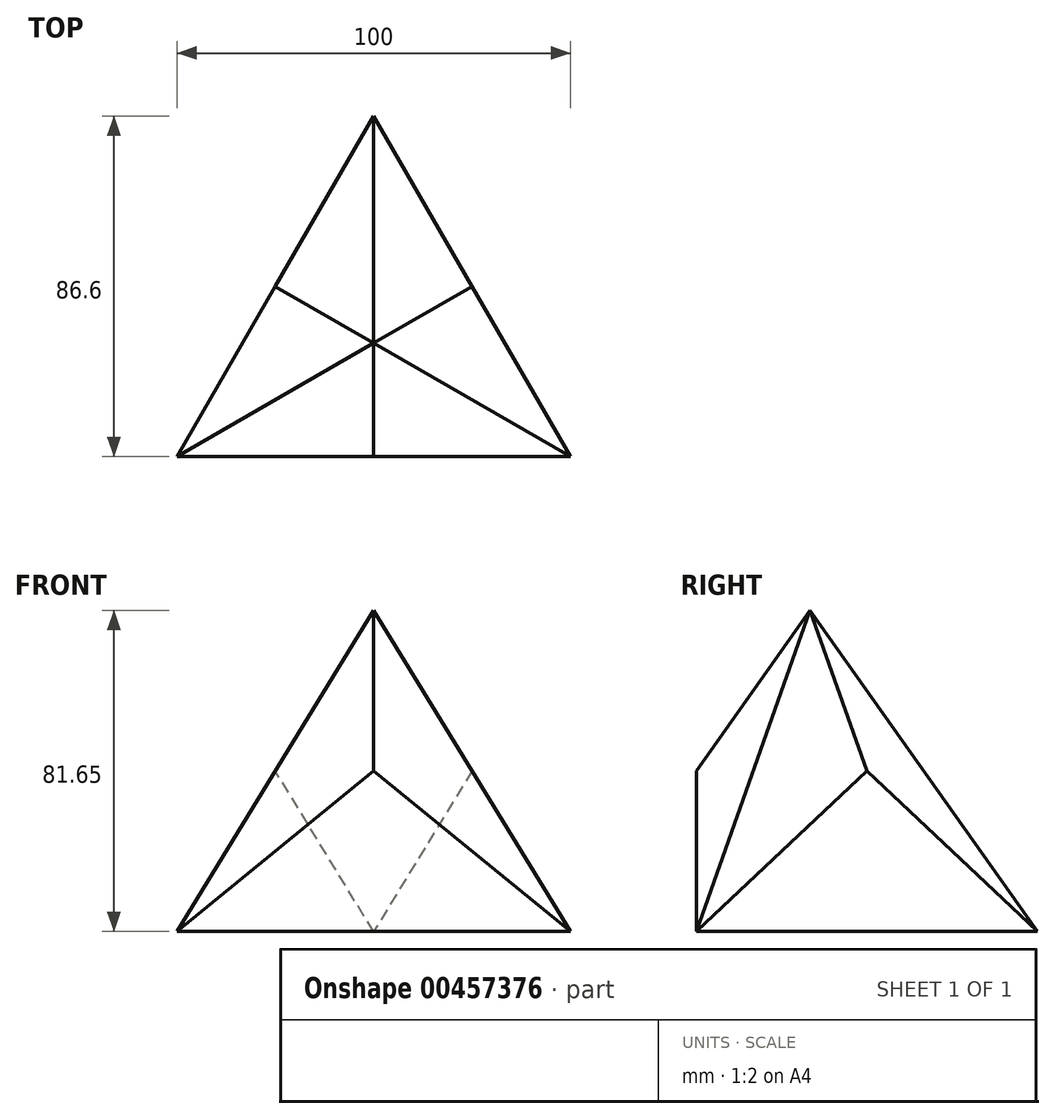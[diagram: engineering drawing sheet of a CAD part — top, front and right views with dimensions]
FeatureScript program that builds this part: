
annotation { "Feature Type Name" : "Feature", "Feature Type Description" : "" }
export const myFeature = defineFeature(function(context is Context, id is Id, definition is map)
    precondition{}
    {
        {
            var Q0;
            Q0=qCreatedBy(makeId("Top.planeOp"),FACE);
            var sketch = newSketch(context, id + "F0", { "sketchPlane" : qUnion([Q0])});
            skLineSegment(sketch, "E0.bottom", {"start": v(50, -43.3) * mm, "end": v(-50, -43.3) * mm});
            skLineSegment(sketch, "E0.top", {"start": v(50, 43.3) * mm, "end": v(-50, 43.3) * mm});
            skLineSegment(sketch, "E0.left", {"start": v(50, -43.3) * mm, "end": v(50, 43.3) * mm});
            skLineSegment(sketch, "E0.right", {"start": v(-50, -43.3) * mm, "end": v(-50, 43.3) * mm});
            skPoint(sketch, "E0.middle", {"position": v(0, 0) * mm});
            skLineSegment(sketch, "E1", {"start": v(-50, -43.3) * mm, "end": v(0, 43.3) * mm});
            skLineSegment(sketch, "E2", {"start": v(0, 43.3) * mm, "end": v(50, -43.3) * mm});
            skLineSegment(sketch, "E3", {"start": v(-25, 0) * mm, "end": v(0, -43.3) * mm});
            skLineSegment(sketch, "E4", {"start": v(0, -43.3) * mm, "end": v(25, 0) * mm});
            skLineSegment(sketch, "E5", {"start": v(25, 0) * mm, "end": v(-25, 0) * mm});
            skLineSegment(sketch, "E6", {"start": v(-25, 0) * mm, "end": v(50, -43.3) * mm, "construction": true});
            skLineSegment(sketch, "E7", {"start": v(25, 0) * mm, "end": v(-50, -43.3) * mm, "construction": true});
            skPoint(sketch, "E8", {"position": v(0, -14.43) * mm});
            skSolve(sketch);
        }
        {
            var Q0;
            {var subQ3=sQuery(id+"F0.wireOp",EDGE,"E5");Q0=makeQuery(id+"F0.imprint","IMPRINT",FACE,{"disambiguationData":[TD([[makeQuery(id+"F0.imprint","IMPRINT",EDGE,{"derivedFrom":subQ3}),-1.0]])]});}
            var Q1;
            Q1=makeQuery(id+"F0.imprint","IMPRINT",FACE,{"disambiguationData":[TD([[makeQuery(id+"F0.imprint","IMPRINT",EDGE,{"derivedFrom":sQuery(id+"F0.wireOp",EDGE,"E3")}),1.0]])]});
            var Q2;
            {var subQ3=sQuery(id+"F0.wireOp",EDGE,"E3");Q2=makeQuery(id+"F0.imprint","IMPRINT",FACE,{"disambiguationData":[TD([[makeQuery(id+"F0.imprint","IMPRINT",EDGE,{"derivedFrom":subQ3}),-1.0]])]});}
            var Q3;
            {var subQ3=sQuery(id+"F0.wireOp",EDGE,"E4");Q3=makeQuery(id+"F0.imprint","IMPRINT",FACE,{"disambiguationData":[TD([[makeQuery(id+"F0.imprint","IMPRINT",EDGE,{"derivedFrom":subQ3}),-1.0]])]});}
            extrude(context, id + "F1", {"entities" : qUnion([Q0, Q1, Q2, Q3]), "depth" : sqrt(20000 / 3) * mm});
        }
        {
            var Q0;
            Q0=makeQuery(id+"F1.opExtrude","SWEPT_FACE",FACE,{"disambiguationData":[OSD([sQuery(id+"F0.wireOp",EDGE,"E0.bottom")])]});
            var sketch = newSketch(context, id + "F2", { "sketchPlane" : qUnion([Q0])});
            skLineSegment(sketch, "E9", {"start": v(-50, 0) * mm, "end": v(0, 81.65) * mm});
            skLineSegment(sketch, "E10", {"start": v(0, 81.65) * mm, "end": v(50, 0) * mm});
            skLineSegment(sketch, "E11", {"start": v(50, 0) * mm, "end": v(-50, 0) * mm});
            skSolve(sketch);
        }
        {
            var Q0;
            Q0=makeQuery(id+"F1.opExtrude","SWEPT_FACE",FACE,{"disambiguationData":[OSD([sQuery(id+"F0.wireOp",EDGE,"E2")])]});
            var sketch = newSketch(context, id + "F3", { "sketchPlane" : qUnion([Q0])});
            skLineSegment(sketch, "E12", {"start": v(-62.5, 0) * mm, "end": v(-12.5, 81.65) * mm});
            skLineSegment(sketch, "E13", {"start": v(-12.5, 81.65) * mm, "end": v(37.5, 0) * mm});
            skLineSegment(sketch, "E14", {"start": v(37.5, 0) * mm, "end": v(-62.5, 0) * mm});
            skSolve(sketch);
        }
        {
            var Q0;
            Q0=makeQuery(id+"F1.opExtrude","SWEPT_FACE",FACE,{"disambiguationData":[OSD([sQuery(id+"F0.wireOp",EDGE,"E1")])]});
            var sketch = newSketch(context, id + "F4", { "sketchPlane" : qUnion([Q0])});
            skLineSegment(sketch, "E15", {"start": v(-37.5, 0) * mm, "end": v(12.5, 81.65) * mm});
            skLineSegment(sketch, "E16", {"start": v(12.5, 81.65) * mm, "end": v(62.5, 0) * mm});
            skLineSegment(sketch, "E17", {"start": v(62.5, 0) * mm, "end": v(-37.5, 0) * mm});
            skSolve(sketch);
        }
        {
            var Q0;
            {var subQ0=sQuery(id+"F4.wireOp",EDGE,"E15");Q0=makeQuery(id+"F4.imprint","IMPRINT",FACE,{"disambiguationData":[TD([[makeQuery(id+"F4.imprint","IMPRINT",EDGE,{"derivedFrom":subQ0}),1.0]])]});}
            var Q1;
            {var subQ0=sQuery(id+"F4.wireOp",EDGE,"E16");Q1=makeQuery(id+"F4.imprint","IMPRINT",FACE,{"disambiguationData":[TD([[makeQuery(id+"F4.imprint","IMPRINT",EDGE,{"derivedFrom":subQ0}),1.0]])]});}
            extrude(context, id + "F5", {"entities" : qUnion([Q0, Q1]), "operationType" : NewBodyOperationType.REMOVE, "oppositeDirection" : true, "depth" : 100 * mm});
        }
        {
            var Q0;
            {var subQ0=sQuery(id+"F2.wireOp",EDGE,"E9");Q0=makeQuery(id+"F2.imprint","IMPRINT",FACE,{"disambiguationData":[TD([[makeQuery(id+"F2.imprint","IMPRINT",EDGE,{"derivedFrom":subQ0}),1.0]])]});}
            var Q1;
            {var subQ0=sQuery(id+"F2.wireOp",EDGE,"E10");Q1=makeQuery(id+"F2.imprint","IMPRINT",FACE,{"disambiguationData":[TD([[makeQuery(id+"F2.imprint","IMPRINT",EDGE,{"derivedFrom":subQ0}),1.0]])]});}
            extrude(context, id + "F6", {"entities" : qUnion([Q0, Q1]), "operationType" : NewBodyOperationType.REMOVE, "oppositeDirection" : true, "depth" : 100 * mm});
        }
        {
            var Q0;
            {var subQ0=sQuery(id+"F3.wireOp",EDGE,"E12");Q0=makeQuery(id+"F3.imprint","IMPRINT",FACE,{"disambiguationData":[TD([[makeQuery(id+"F3.imprint","IMPRINT",EDGE,{"derivedFrom":subQ0}),1.0]])]});}
            var Q1;
            {var subQ0=sQuery(id+"F3.wireOp",EDGE,"E13");Q1=makeQuery(id+"F3.imprint","IMPRINT",FACE,{"disambiguationData":[TD([[makeQuery(id+"F3.imprint","IMPRINT",EDGE,{"derivedFrom":subQ0}),1.0]])]});}
            extrude(context, id + "F7", {"entities" : qUnion([Q0, Q1]), "operationType" : NewBodyOperationType.REMOVE, "oppositeDirection" : true, "depth" : 100 * mm});
        }
    });
